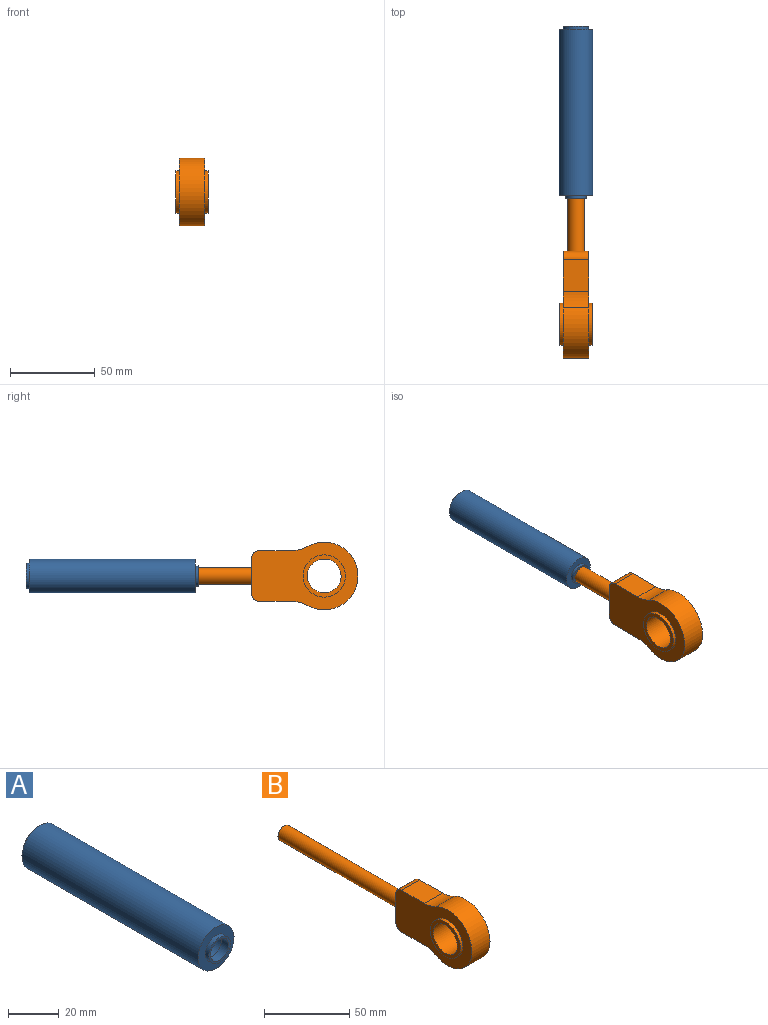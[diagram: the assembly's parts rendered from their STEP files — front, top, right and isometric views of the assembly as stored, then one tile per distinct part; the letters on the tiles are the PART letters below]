
ASSEMBLY  parts=2 mates=1
PART A: 11 faces, bbox 20x102x20 mm
  f0: cylinder r=5mm len=10mm, axis (0,-1,0), area 125.7mm2, adj f2,f3
  f1: cylinder r=6mm len=12mm, axis (0,-1,0), area 75.4mm2, adj f3,f7
  f2: plane 12x12mm, normal (0,1,0), area 34.6mm2, adj f0,f4
  f3: plane 12x12mm, normal (0,-1,0), area 34.6mm2, adj f0,f1
  f4: cylinder r=6mm len=96mm, axis (0,-1,0), area 3619.1mm2, adj f2,f10
  f5: cylinder r=10mm len=98mm, axis (0,-1,0), area 6157.5mm2, adj f6,f7
  f6: plane 20x20mm, normal (0,1,0), area 137.4mm2, adj f5,f9
  f7: plane 20x20mm, normal (0,-1,0), area 201.1mm2, adj f1,f5
  f8: plane 15x15mm, normal (0,1,0), area 176.7mm2, adj f9
  f9: cylinder r=7.5mm len=15mm, axis (0,-1,0), area 94.2mm2, adj f6,f8
  f10: plane 12x12mm, normal (0,-1,0), area 113.1mm2, adj f4
PART B: 17 faces, bbox 19x163.2x40 mm
  f0: plane 18.86x15mm, normal (0,0,-1), area 283mm2, adj f5,f6,f13,f16
  f1: plane 20x15mm, normal (0,1,0), area 221.5mm2, adj f5,f6,f11,f13,f14
  f2: plane 18.86x15mm, normal (0,0,1), area 283mm2, adj f5,f6,f14,f15
  f3: cylinder r=20mm len=40mm, axis (-1,0,0), area 1245.7mm2, adj f5,f6,f15,f16
  f4: cylinder r=10mm len=20mm, axis (-1,0,0), area 1193.8mm2, adj f8,f10
  f5: plane 63.23x40mm, normal (1,0,0), area 1520.4mm2, adj f0,f1,f2,f3,f7,f13,f14,f15
  f6: plane 63.23x40mm, normal (-1,0,0), area 1520.4mm2, adj f0,f1,f2,f3,f9,f13,f14,f15
  f7: cylinder r=12.5mm len=25mm, axis (-1,0,0), area 157.1mm2, adj f5,f8
  f8: plane 25x25mm, normal (1,0,0), area 176.7mm2, adj f4,f7
  f9: cylinder r=12.5mm len=25mm, axis (1,0,0), area 157.1mm2, adj f6,f10
  f10: plane 25x25mm, normal (-1,0,0), area 176.7mm2, adj f4,f9
  f11: cylinder r=5mm len=100mm, axis (0,-1,0), area 3141.6mm2, adj f1,f12
  f12: plane 10x10mm, normal (0,1,0), area 78.5mm2, adj f11
  f13: cylinder r=5mm len=15mm, axis (1,0,0), area 117.8mm2, adj f0,f1,f5,f6
  f14: cylinder r=5mm len=15mm, axis (-1,0,0), area 117.8mm2, adj f1,f2,f5,f6
  f15: cylinder r=20mm len=15mm, axis (-1,0,0), area 151.6mm2, adj f2,f3,f5,f6
  f16: cylinder r=20mm len=15mm, axis (-1,0,0), area 151.6mm2, adj f0,f3,f5,f6
PLACE A at identity fixed
PLACE B t=(0,-31.12,0)mm
MATE slider B.f11 <-> A.f0  axis (0,1,0) through (7.5,68.88,15)mm
